# Revit family: Kessel 8740028 en
name_source: partatom
category: Plumbing Fixtures
revit_build: Autodesk Revit Architecture 2014 (Build: 20130308_1515(x64)
units: mm (PartAtom-declared; Revit-internal decimal feet)

## types (1)
- Kessel 8740028 en
    <1.010.00.2> Number of the part of the guideline = 4
    <1.010.00.3> Issue date (month) of the guideline = 201410
    <1.010.00.4> Manufacturer name = Kessel
    <1.010.00.5> Revision date of the file = 20190228
    <1.800.00.3> BS number = 10000100000000000000000000000000000000000000000058000
    <1.800.00.4> Comment field = Chamber module CO 1000 below ground installation, access CO 800, 1396-1645 mm, Class A
    <1.810.00.3> Manufacturer’s reference number = 8740028
    <1.810.00.4> DATANORM number = 8740028
    <1.810.00.6> GTIN number = 4026092065433
    <1.960/3L.00.8> Link (URL) = http://www.kessel.de
    <4.100.00.4> Area of application = Accessories
    <4.110.00.4> Model series = Accessories
    <4.700.00.10> Star / delta starting circuit with three-phase connection or three-phase current = no
    <4.700.00.46> vertical installation = no
    <4.700.00.47> outdoor installation = no
    <4.700.00.48> ATEX = no
    <4.700.00.49> protection class = protection class I
    <4.700.00.4> Product name = Chamber module CO 1000 below ground installation, access CO 800, 1396-1645 mm, Class A
    <4.700.00.50> motor protection = no
    CONNECTOR0_ref_dX = 501 mm
    CONNECTOR0_ref_dZ = 1206 mm
    CONNECTOR1_ref_dY = 501 mm
    CONNECTOR1_ref_dZ = 1206 mm
    CONNECTOR2_ref_dZ = 1 mm  [stored 0.00328084 ft]
    Manufacturer = Kessel
    Model = 8740028
    URL = www.kessel.com

note: [stored X ft] marks values corroborated as IEEE doubles in the binary element streams (Revit-internal decimal feet)
